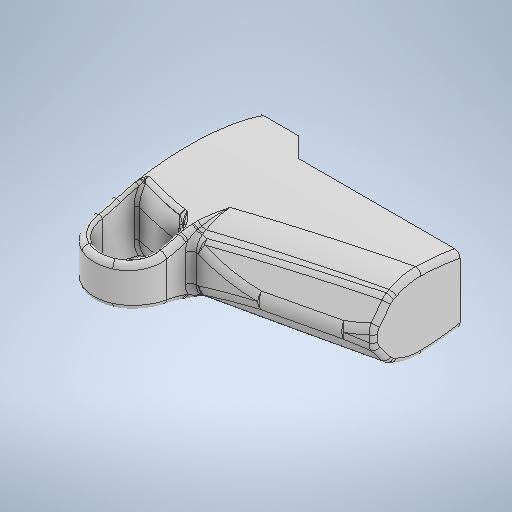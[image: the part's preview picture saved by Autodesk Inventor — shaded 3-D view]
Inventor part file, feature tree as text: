
AUTODESK INVENTOR PART (.ipt)
format: ipt  version: 2025 (Build 290162000, 162)  size: 1,548,288 bytes
history: native  units: in
note: dims shown in document units (in); Inventor stores cm internally (conversion verified against a paired STEP export)
features: fillet x13, extrude x7, other x6, sketch x5, chamfer x5, projected_geometry x3, mirror x1
ambient origin geometry x8: Origin, YZ Plane, XZ Plane, XY Plane, X Axis, Y Axis, Z Axis, Center Point
bodies: Body1 (feature_tree)
feature tree (40):
  other  "ソリッド1"
  sketch  "スケッチ1"
  extrude  "押し出し1"  Depth=3.3465in
  sketch  "スケッチ4"
  extrude  "押し出し4"  Depth=0.2756in
  extrude  "押し出し5"  Depth=9.8425in
  extrude  "押し出し6"  Depth=0.8661in TaperAngle=0.0deg
  extrude  "押し出し7"  Depth=0.8268in
  chamfer  "面取り1"  Distance=0.1181in
  chamfer  "面取り2"  Distance=0.1181in
  chamfer  "面取り3"  Distance=1.8504in
  chamfer  "面取り4"  Distance=1.1024in
  other  "作業平面3"
  other  "作業平面5"
  extrude  "押し出し8"  Depth=1.5354in
  other  "作業平面6"
  mirror  "ミラー1"
  chamfer  "面取り5"  Distance=3.3465in
  extrude  "押し出し9"  Depth=3.3465in TaperAngle=0.0deg
  fillet  "フィレット27"  Radius=3.3465in
  fillet  "フィレット28"  Radius=3.3465in
  fillet  "フィレット29"  Radius=0.1181in
  fillet  "フィレット30"  Radius=0.1181in
  fillet  "フィレット32"  Radius=0.1181in
  fillet  "フィレット35"  Radius=0.1181in
  fillet  "フィレット36"  Radius=0.3937in
  fillet  "フィレット37"  Radius=0.1575in
  fillet  "フィレット38"  Radius=0.5906in
  fillet  "フィレット42"  [1 undecoded]
  fillet  "フィレット43"  Radius=0.3937in
  fillet  "フィレット44"  Radius=1.9685in
  fillet  "フィレット45"  Radius=2.0866in
  projected_geometry  "投影ループ2"
  sketch  "スケッチ5"
  projected_geometry  "投影ループ3"
  sketch  "スケッチ6"
  projected_geometry  "投影ループ4"
  other  "作業平面2"
  other  "作業平面4"
  sketch  "スケッチ7"
note: 1 required parameter value undecoded (feature->parameter linkage not recoverable at this tier; creation-order binding heuristic only, values carry confidence <= 0.55)
